# Revit family: NBS_Allermuir_OffcChrs_Cardita_SideChair
name_source: partatom
category: Furniture
revit_build: Autodesk Revit 2018 (Build: 20190510_1515(x64)
units: mm (PartAtom-declared; Revit-internal decimal feet)

## family parameters
Always vertical = Yes
Cut with Voids When Loaded = No
Room Calculation Point = No
Shared = No
Work Plane-Based = No

## types (1)
- Cardita_SideChair_CRD01
    AssetType = Movable
    BIMObjectName = NBS_Allermuir_OfficeChairs_Cardita_SideChair_CRD01
    Category = Pr_40_50_12_57:Office chairs
    ChairMaterial = NBS_Allermuir_Fabric
    Color = White as Snow, Back to Black, Slate Grey, Smoke Grey, Vintage Red, Ruby Red, Fern Green, Peacock Green
    Description = Side chair on wood legs
    DurationUnit = year
    ExpectedLife = 10
    Features = Molded shell, Fully upholstered with luxury quilt detail, Solid Ash legs with a clear finish, Plastic glides, Solid Ash legs can be stained or colorwashed, Plastic glides with felt
    Finish = White as Snow, Back to Black, Slate Grey, Smoke Grey, Vintage Red, Ruby Red, Fern Green, Peacock Green
    FrameFinish = Clear
    FrameMaterial = Solid Ash
    HighestSeatingHeight = 0 mm  [stored 0 ft]
    IfcExportAs = IfcFurnitureType
    IfcExportType = CHAIR
    IsBuiltIn = No
    LegMaterial = NBS_Allermuir_Ash_ClearFinish
    LowestSeatingHeight = 0 mm  [stored 0 ft]
    ManufacturerName = Allermuir
    ManufacturerURL = www.allermuir.co.uk
    Material = Wood, steel
    ModelNumber = CRD01
    ModelReference = Cardita_SideChair
    NBSCertification = www.nationalbimlibrary.com/cert/hqgs5awo
    NBSDescription = Office chairs
    NBSReference = 45-35-20/330
    Name = OfficeChairs_CRD01_Cardita_Allermuir
    NominalDepth = 625 mm
    NominalHeight = 830 mm  [stored 2.7231 ft]
    NominalLength = 550 mm
    NominalWidth = 550 mm
    ProductInformation = https://www.allermuir.com
    SeatDepth = 440 mm
    SeatWidth = 480 mm
    SeatingHeight = 440 mm
    Size = 625 x 830 x 550 mm
    Status = UNSET
    Style = Chair
    SustainabilityPerformance = 99% recyclable
    Uniclass2015Code = Pr_40_50_12_57
    Uniclass2015Title = Office chairs
    Uniclass2015Version = Products v1.15
    Version = 1
    WarrantyDescription = Allermuir warrant that its manufactured products are free from manufacturing defects - in materials or workmanship - for a period of five (5) years. , Allermuir will repair, or replace (at Allermuir's sole discretion) with comparable free of charge materials / components, any product / component which fails under normal use in a single shift environment, as a result of a defect in the materials and/ or workmanship
    WarrantyDurationParts = 5
    WarrantyDurationUnit = year
    WoodStains = White Oak, American Cherry, American Walnut, Dark walnut, Wenge

note: [stored X ft] marks values corroborated as IEEE doubles in the binary element streams (Revit-internal decimal feet)

## geometry (parser evidence)
native form markers: Sweep x2
no freeform markers — native parametric forms only
